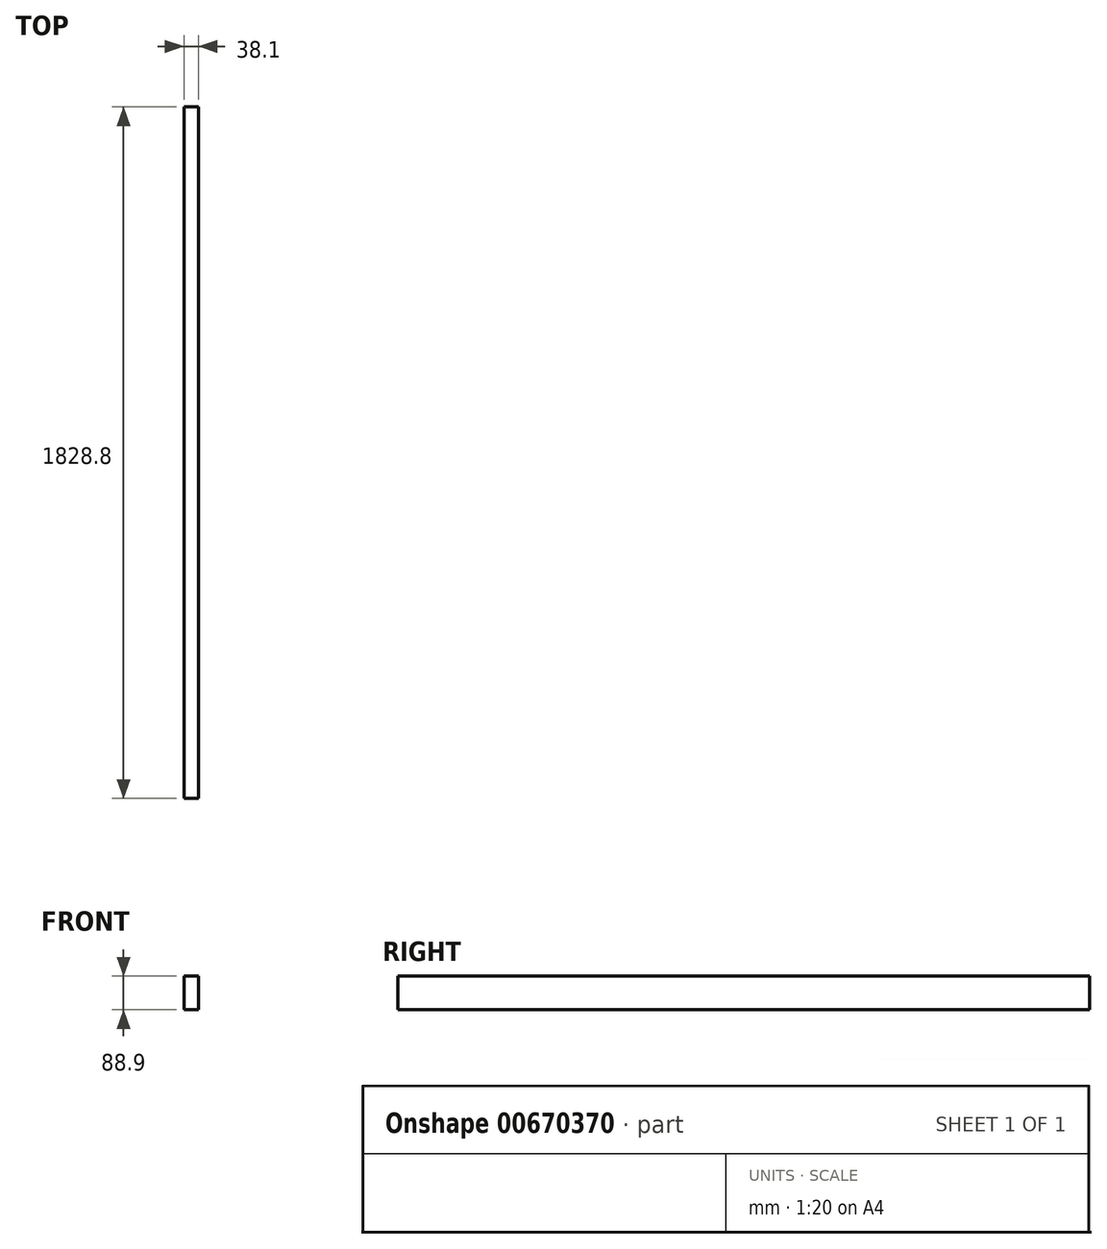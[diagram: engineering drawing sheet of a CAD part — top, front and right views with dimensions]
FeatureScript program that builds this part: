
annotation { "Feature Type Name" : "Feature", "Feature Type Description" : "" }
export const myFeature = defineFeature(function(context is Context, id is Id, definition is map)
    precondition{}
    {
        {
            var Q0;
            Q0=qCreatedBy(makeId("Front.planeOp"),FACE);
            var sketch = newSketch(context, id + "F0", { "sketchPlane" : qUnion([Q0])});
            skLineSegment(sketch, "E0.bottom", {"start": v(-38.1, -10.7) * mm, "end": v(0, -10.7) * mm});
            skLineSegment(sketch, "E0.top", {"start": v(-38.1, 78.2) * mm, "end": v(0, 78.2) * mm});
            skLineSegment(sketch, "E0.left", {"start": v(-38.1, -10.7) * mm, "end": v(-38.1, 78.2) * mm});
            skLineSegment(sketch, "E0.right", {"start": v(0, -10.7) * mm, "end": v(0, 78.2) * mm});
            skSolve(sketch);
        }
        {
            var Q0;
            Q0 = qSketchRegion(id + "F0", true);
            extrude(context, id + "F1", {"entities" : qUnion([Q0]), "depth" : 1828.8 * mm, "offsetDistance" : 25.4 * mm});
        }
    });
